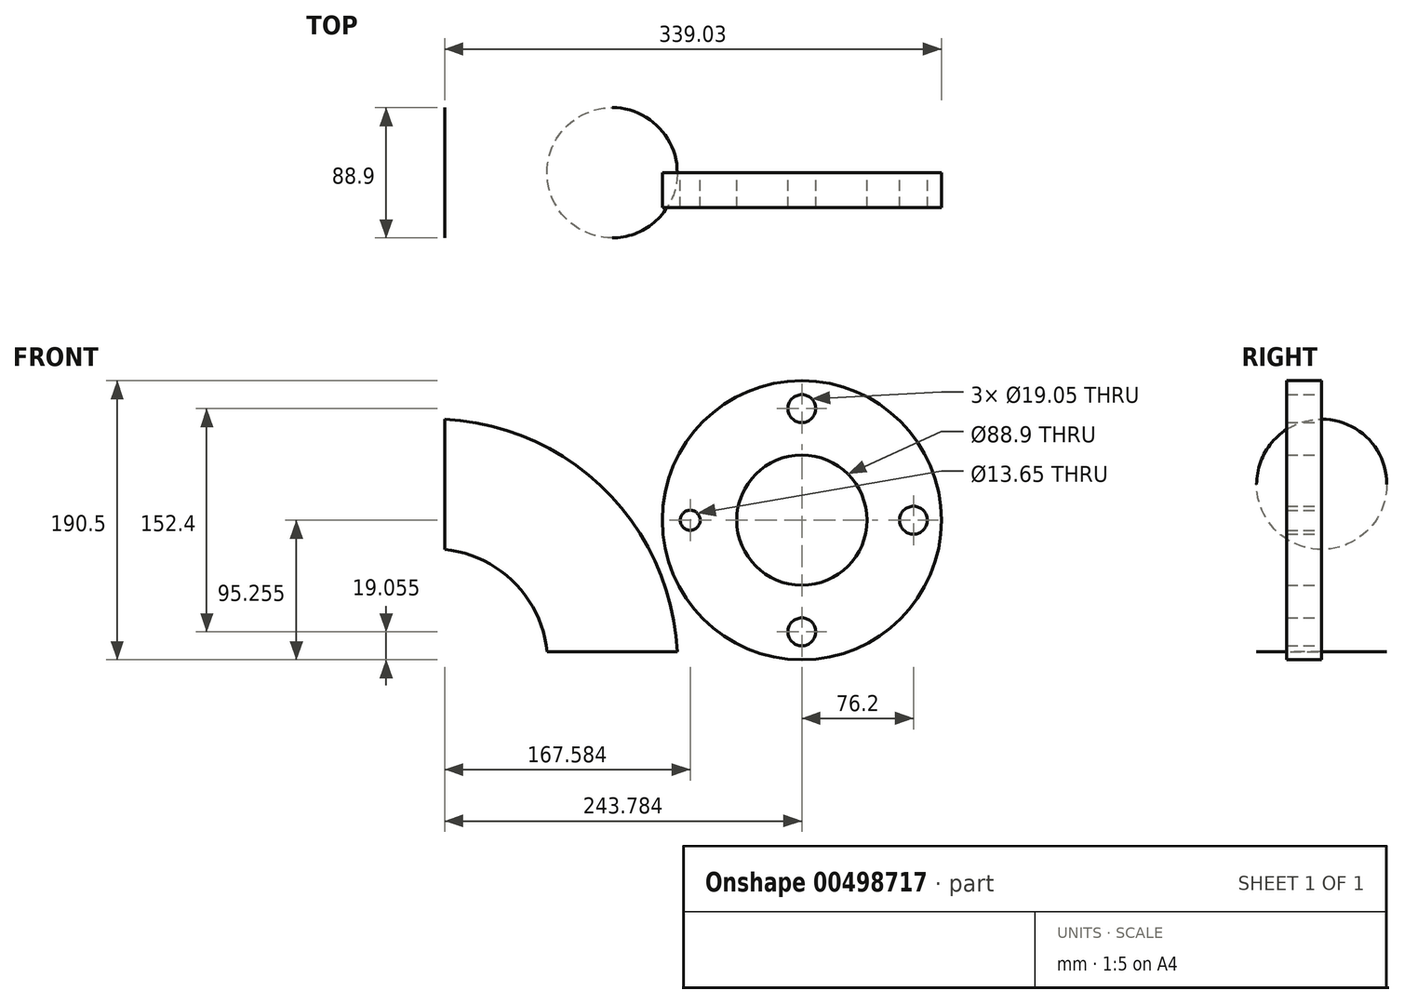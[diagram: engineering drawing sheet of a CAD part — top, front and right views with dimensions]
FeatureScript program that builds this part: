
annotation { "Feature Type Name" : "Feature", "Feature Type Description" : "" }
export const myFeature = defineFeature(function(context is Context, id is Id, definition is map)
    precondition{}
    {
        {
            var Q0;
            Q0=qCreatedBy(makeId("Front.planeOp"),FACE);
            var sketch = newSketch(context, id + "F0", { "sketchPlane" : qUnion([Q0])});
            skLineSegment(sketch, "E0", {"start": v(-141.7, 0) * mm, "end": v(-141.7, 88.9) * mm});
            skLineSegment(sketch, "E1", {"start": v(-71.86, -69.85) * mm, "end": v(-27.4, -69.85) * mm});
            skLineSegment(sketch, "E2", {"start": v(-27.4, -69.85) * mm, "end": v(17.04, -69.85) * mm});
            skPoint(sketch, "E3", {"position": v(-27.4, -69.85) * mm});
            skArc(sketch, "E4", {"start": v(17.04, -69.85) * mm, "mid": v(-31.69, 40.17) * mm, "end": v(-141.7, 88.9) * mm});
            skArc(sketch, "E5", {"start": v(-71.86, -69.85) * mm, "mid": v(-94.35, -22.5) * mm, "end": v(-141.7, 0) * mm});
            skSolve(sketch);
        }
        {
            var Q0;
            Q0=makeQuery(id+"F0.imprint","IMPRINT",FACE,{"disambiguationData":[TD([[makeQuery(id+"F0.imprint","IMPRINT",EDGE,{"derivedFrom":sQuery(id+"F0.wireOp",EDGE,"E0")}),-1.0]])]});
            extrude(context, id + "F1", {"entities" : qUnion([Q0]), "depth" : 88.9 * mm, "symmetric" : true});
        }
        {
            var Q0;
            Q0=makeQuery(id+"F1.opExtrude","CAP_EDGE",EDGE,{"disambiguationData":[OSD([sQuery(id+"F0.wireOp",EDGE,"E4")])],"isStart":false});
            var Q1;
            Q1=makeQuery(id+"F1.opExtrude","CAP_EDGE",EDGE,{"disambiguationData":[OSD([sQuery(id+"F0.wireOp",EDGE,"E5")])],"isStart":false});
            var Q2;
            Q2=makeQuery(id+"F1.opExtrude","CAP_EDGE",EDGE,{"disambiguationData":[OSD([sQuery(id+"F0.wireOp",EDGE,"E4")])],"isStart":true});
            var Q3;
            Q3=makeQuery(id+"F1.opExtrude","CAP_EDGE",EDGE,{"disambiguationData":[OSD([sQuery(id+"F0.wireOp",EDGE,"E5")])],"isStart":true});
            fillet(context, id + "F2", {"entities" : qUnion([Q0, Q1, Q2, Q3]), "radius" : 44.45 * mm, "tangentPropagation" : true, "allowEdgeOverflow" : false});
        }
        {
            var Q0;
            Q0=qCreatedBy(makeId("Front.planeOp"),FACE);
            var sketch = newSketch(context, id + "F3", { "sketchPlane" : qUnion([Q0])});
            skCircle(sketch, "E6", {"center": v(102.07, 19.95) * mm, "radius": 95.25 * mm});
            skCircle(sketch, "E7", {"center": v(102.07, 19.95) * mm, "radius": 44.45 * mm});
            skCircle(sketch, "E8.cCircle", {"center": v(102.07, 19.95) * mm, "radius": 76.2 * mm, "construction": true});
            skPoint(sketch, "E8.0.midPoint", {"position": v(102.07, 96.15) * mm});
            skCircle(sketch, "E9", {"center": v(25.87, 19.95) * mm, "radius": 6.82 * mm});
            skCircle(sketch, "E10", {"center": v(178.27, 19.95) * mm, "radius": 9.53 * mm});
            skCircle(sketch, "E11", {"center": v(102.07, 96.15) * mm, "radius": 9.53 * mm});
            skCircle(sketch, "E12", {"center": v(102.07, -56.25) * mm, "radius": 9.53 * mm});
            skCircle(sketch, "E13", {"center": v(102.07, 19.95) * mm, "radius": 38.1 * mm});
            skSolve(sketch);
        }
        {
            var Q0;
            Q0=makeQuery(id+"F3.imprint","IMPRINT",FACE,{"disambiguationData":[TD([[makeQuery(id+"F3.imprint","IMPRINT",EDGE,{"derivedFrom":sQuery(id+"F3.wireOp",EDGE,"E6")}),1.0]])]});
            extrude(context, id + "F4", {"entities" : qUnion([Q0]), "depth" : 23.88 * mm});
        }
    });
